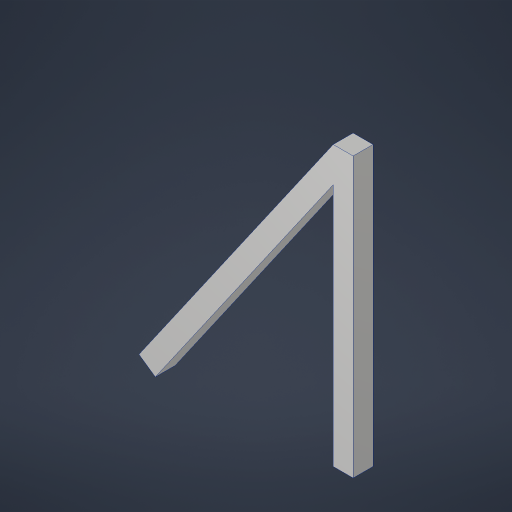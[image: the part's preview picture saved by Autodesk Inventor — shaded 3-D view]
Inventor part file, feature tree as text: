
AUTODESK INVENTOR PART (.ipt)
format: ipt  version: 2023.4 (Build 274418000, 418)  size: 169,472 bytes
history: native  units: in
note: dims shown in document units (in); Inventor stores cm internally (conversion verified against a paired STEP export)
features: extrude x1, sketch x1
ambient origin geometry x8: Origin, YZ Plane, XZ Plane, XY Plane, X Axis, Y Axis, Z Axis, Center Point
bodies: Solid1 (feature_tree)
feature tree (2):
  extrude  "Extrusion1"  Depth=14.0in
  sketch  "Sketch1"  dims[d0=1.0in d1=14.0in d2=1.0in d3=10.75in d4=1.0in d5=0.0in]
